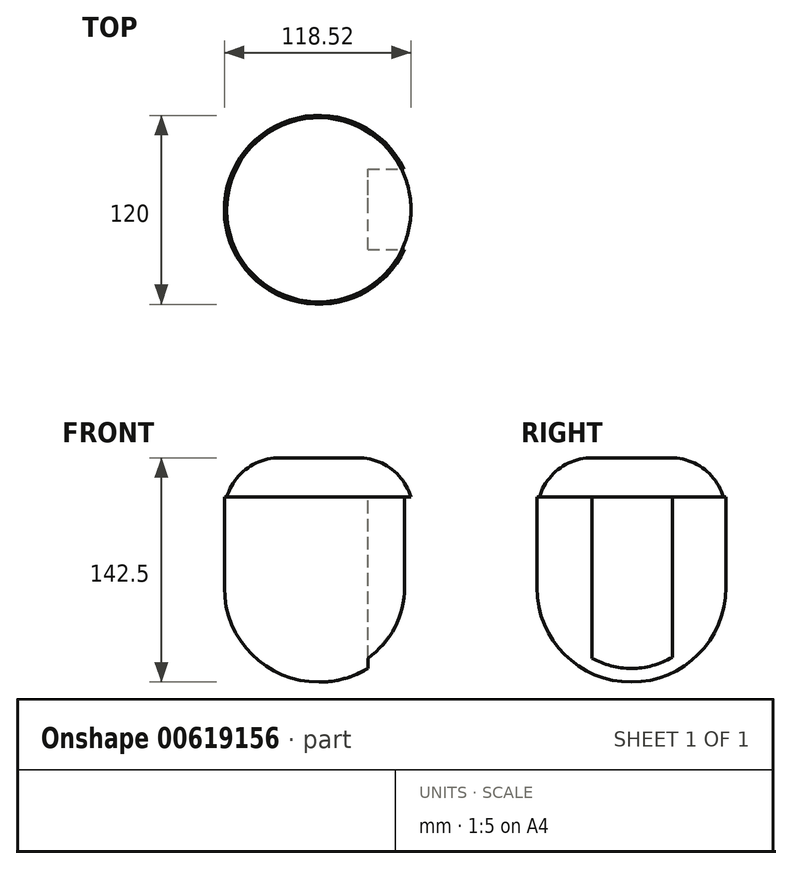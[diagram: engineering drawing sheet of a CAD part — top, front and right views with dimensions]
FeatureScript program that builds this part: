
annotation { "Feature Type Name" : "Feature", "Feature Type Description" : "" }
export const myFeature = defineFeature(function(context is Context, id is Id, definition is map)
    precondition{}
    {
        {
            var Q0;
            Q0=qCreatedBy(makeId("Top.planeOp"),FACE);
            var sketch = newSketch(context, id + "F0", { "sketchPlane" : qUnion([Q0])});
            skCircle(sketch, "E0", {"center": v(0, 0) * mm, "radius": 60 * mm});
            skCircle(sketch, "E1", {"center": v(0, 0) * mm, "radius": 58.5 * mm});
            skSolve(sketch);
        }
        {
            var Q0;
            Q0 = qSketchRegion(id + "F0", true);
            extrude(context, id + "F1", {"entities" : qUnion([Q0]), "oppositeDirection" : true, "depth" : 70 * mm, "offsetDistance" : 25 * mm});
        }
        {
            var Q0;
            Q0=qCreatedBy(makeId("Top.planeOp"),FACE);
            var sketch = newSketch(context, id + "F2", { "sketchPlane" : qUnion([Q0])});
            skCircle(sketch, "E2", {"center": v(0, 0) * mm, "radius": 60 * mm});
            skSolve(sketch);
        }
        {
            var Q0;
            Q0 = qSketchRegion(id + "F2", true);
            extrude(context, id + "F3", {"entities" : qUnion([Q0]), "operationType" : NewBodyOperationType.ADD, "depth" : 25 * mm, "offsetDistance" : 25 * mm});
        }
        {
            var Q0;
            Q0=makeQuery(id+"F3.opExtrude","CAP_FACE",FACE,{"disambiguationData":[OSD([sQuery(id+"F2.wireOp",EDGE,"E2")])],"isStart":false});
            fillet(context, id + "F4", {"entities" : qUnion([Q0]), "radius" : 35.1 * mm, "tangentPropagation" : true, "allowEdgeOverflow" : false});
        }
        {
            var Q0;
            Q0=qCreatedBy(makeId("Top.planeOp"),FACE);
            var sketch = newSketch(context, id + "F5", { "sketchPlane" : qUnion([Q0])});
            skCircle(sketch, "E3", {"center": v(0, 0) * mm, "radius": 60 * mm});
            skSolve(sketch);
        }
        {
            var Q0;
            Q0=makeQuery(id+"F5.imprint","IMPRINT",FACE,{"disambiguationData":[TD([[makeQuery(id+"F5.imprint","IMPRINT",EDGE,{"derivedFrom":sQuery(id+"F5.wireOp",EDGE,"E3")}),1.0]])]});
            extrude(context, id + "F6", {"entities" : qUnion([Q0]), "operationType" : NewBodyOperationType.ADD, "oppositeDirection" : true, "depth" : 117.5 * mm, "offsetDistance" : 25 * mm});
        }
        {
            var Q0;
            Q0=makeQuery(id+"F6.opExtrude","CAP_EDGE",EDGE,{"disambiguationData":[OSD([sQuery(id+"F5.wireOp",EDGE,"E3")])],"isStart":false});
            var Q1;
            Q1=makeQuery(id+"F6.opExtrude","CAP_FACE",FACE,{"disambiguationData":[OSD([sQuery(id+"F5.wireOp",EDGE,"E3")])],"isStart":false});
            var Q2;
            {var subQ0=sQuery(id+"F2.wireOp",EDGE,"E2");Q2=makeQuery(id+"F4.opFillet","BLEND_EDGE",EDGE,{"blendedFrom":[makeQuery(id+"F3.opExtrude","CAP_EDGE",EDGE,{"disambiguationData":[OSD([subQ0])],"isStart":false}),makeQuery(id+"F3.opExtrude","CAP_FACE",FACE,{"disambiguationData":[OSD([subQ0])],"isStart":false})],"blendedInto":[makeQuery(id+"F3.opExtrude","CAP_FACE",FACE,{"disambiguationData":[OSD([subQ0])],"isStart":false})]});}
            fillet(context, id + "F7", {"entities" : qUnion([Q0, Q1, Q2]), "radius" : 60 * mm, "tangentPropagation" : true, "allowEdgeOverflow" : false});
        }
        {
            var Q0;
            Q0=qCreatedBy(makeId("Top.planeOp"),FACE);
            var sketch = newSketch(context, id + "F8", { "sketchPlane" : qUnion([Q0])});
            skLineSegment(sketch, "E4.bottom", {"start": v(31.08, -25.06) * mm, "end": v(64.8, -25.06) * mm});
            skLineSegment(sketch, "E4.top", {"start": v(31.08, 26.02) * mm, "end": v(64.8, 26.02) * mm});
            skLineSegment(sketch, "E4.left", {"start": v(31.08, -25.06) * mm, "end": v(31.08, 26.02) * mm});
            skLineSegment(sketch, "E4.right", {"start": v(64.8, -25.06) * mm, "end": v(64.8, 26.02) * mm});
            skSolve(sketch);
        }
        {
            var Q0;
            Q0=makeQuery(id+"F8.imprint","IMPRINT",FACE,{"disambiguationData":[TD([[makeQuery(id+"F8.imprint","IMPRINT",EDGE,{"derivedFrom":sQuery(id+"F8.wireOp",EDGE,"E4.bottom")}),1.0]])]});
            extrude(context, id + "F9", {"entities" : qUnion([Q0]), "operationType" : NewBodyOperationType.REMOVE, "oppositeDirection" : true, "depth" : 133 * mm, "offsetDistance" : 25 * mm});
        }
    });
